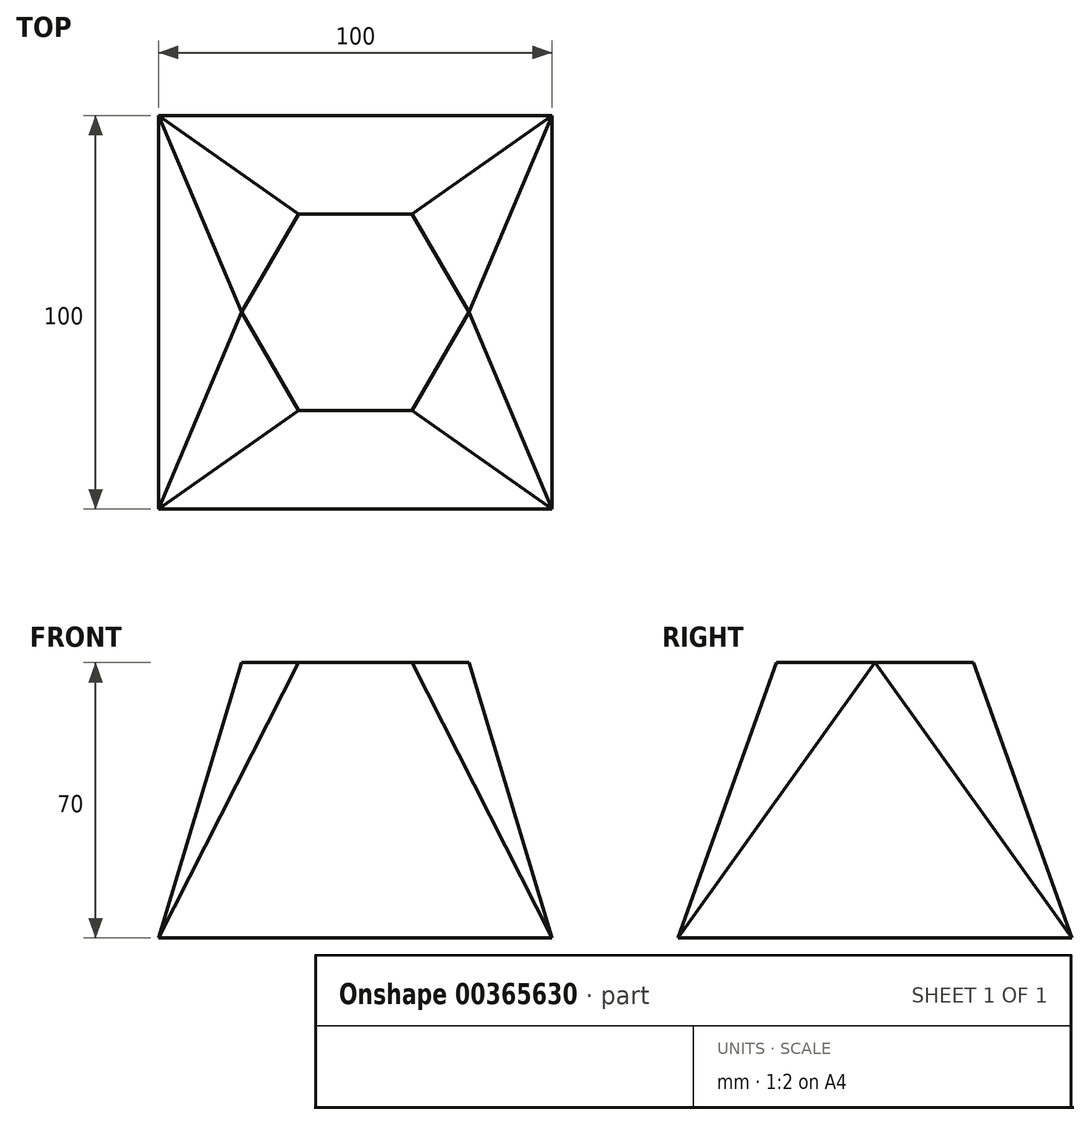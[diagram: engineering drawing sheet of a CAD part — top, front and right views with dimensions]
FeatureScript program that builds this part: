
annotation { "Feature Type Name" : "Feature", "Feature Type Description" : "" }
export const myFeature = defineFeature(function(context is Context, id is Id, definition is map)
    precondition{}
    {
        {
            var Q0;
            Q0=qCreatedBy(makeId("Top.planeOp"),FACE);
            cPlane(context, id + "F0", {"entities" : qUnion([Q0]), "cplaneType" : CPlaneType.OFFSET, "offset" : 70 * mm, "width" : 150 * mm, "height" : 150 * mm});
        }
        {
            var Q0;
            Q0=qCreatedBy(id+"F0.planeOp",FACE);
            var sketch = newSketch(context, id + "F1", { "sketchPlane" : qUnion([Q0])});
            skCircle(sketch, "E0.cCircle", {"center": v(0, 0) * mm, "radius": 25 * mm, "construction": true});
            skLineSegment(sketch, "E0.0", {"start": v(-14.43, 25) * mm, "end": v(14.43, 25) * mm});
            skLineSegment(sketch, "E0.1", {"start": v(14.43, 25) * mm, "end": v(28.87, 0) * mm});
            skLineSegment(sketch, "E0.2", {"start": v(28.87, 0) * mm, "end": v(14.43, -25) * mm});
            skLineSegment(sketch, "E0.3", {"start": v(14.43, -25) * mm, "end": v(-14.43, -25) * mm});
            skLineSegment(sketch, "E0.4", {"start": v(-14.43, -25) * mm, "end": v(-28.87, 0) * mm});
            skLineSegment(sketch, "E0.5", {"start": v(-28.87, 0) * mm, "end": v(-14.43, 25) * mm});
            skPoint(sketch, "E0.0.midPoint", {"position": v(0, 25) * mm});
            skLineSegment(sketch, "E1", {"start": v(-14.43, 25) * mm, "end": v(-14.43, -25) * mm});
            skLineSegment(sketch, "E2", {"start": v(14.43, 25) * mm, "end": v(14.43, -25) * mm});
            skSolve(sketch);
        }
        {
            var Q0;
            Q0=qCreatedBy(makeId("Top.planeOp"),FACE);
            var sketch = newSketch(context, id + "F2", { "sketchPlane" : qUnion([Q0])});
            skLineSegment(sketch, "E3.bottom", {"start": v(-50, 50) * mm, "end": v(50, 50) * mm});
            skLineSegment(sketch, "E3.top", {"start": v(-50, -50) * mm, "end": v(50, -50) * mm});
            skLineSegment(sketch, "E3.left", {"start": v(-50, 50) * mm, "end": v(-50, -50) * mm});
            skLineSegment(sketch, "E3.right", {"start": v(50, 50) * mm, "end": v(50, -50) * mm});
            skPoint(sketch, "E3.middle", {"position": v(0, 0) * mm});
            skSolve(sketch);
        }
        {
            var Q0;
            Q0=makeQuery(id+"F1.imprint","IMPRINT",FACE,{"disambiguationData":[TD([[makeQuery(id+"F1.imprint","IMPRINT",EDGE,{"derivedFrom":sQuery(id+"F1.wireOp",EDGE,"E0.0")}),-1.0]])]});
            var Q1;
            Q1=makeQuery(id+"F2.imprint","IMPRINT",FACE,{"disambiguationData":[TD([[makeQuery(id+"F2.imprint","IMPRINT",EDGE,{"derivedFrom":sQuery(id+"F2.wireOp",EDGE,"E3.bottom")}),-1.0]])]});
            loft(context, id + "F3", {"sheetProfilesArray" : [{ "sheetProfileEntities" : qUnion([Q0]) }, { "sheetProfileEntities" : qUnion([Q1]) }]});
        }
        {
            var Q1;
            Q1=makeQuery(id+"F1.imprint","IMPRINT",FACE,{"disambiguationData":[TD([[makeQuery(id+"F1.imprint","IMPRINT",EDGE,{"derivedFrom":sQuery(id+"F1.wireOp",EDGE,"E0.4")}),-1.0]])]});
            var Q2;
            Q2=makeQuery(id+"F3.opLoft","MID_CAP_VERTEX",VERTEX,{"disambiguationData":[OSD([sQuery(id+"F2.wireOp",EDGE,"E3.bottom"),sQuery(id+"F2.wireOp",EDGE,"E3.left")])],"capPos":1.0});
            loft(context, id + "F4", {"operationType" : NewBodyOperationType.ADD, "sheetProfilesArray" : [{ "sheetProfileEntities" : qUnion([Q1]) }, { "sheetProfileEntities" : qUnion([Q2]) }]});
        }
        {
            var Q1;
            Q1=makeQuery(id+"F4.opLoft","SWEPT_FACE",FACE,{"disambiguationData":[OSD([sQuery(id+"F1.wireOp",EDGE,"E0.3"),sQuery(id+"F1.wireOp",EDGE,"E0.4"),sQuery(id+"F1.wireOp",EDGE,"E0.5"),sQuery(id+"F1.wireOp",EDGE,"E1")])]});
            var Q2;
            Q2=makeQuery(id+"F3.opLoft","MID_CAP_VERTEX",VERTEX,{"disambiguationData":[OSD([sQuery(id+"F2.wireOp",EDGE,"E3.top"),sQuery(id+"F2.wireOp",EDGE,"E3.left")])],"capPos":1.0});
            loft(context, id + "F5", {"operationType" : NewBodyOperationType.ADD, "sheetProfilesArray" : [{ "sheetProfileEntities" : qUnion([Q1]) }, { "sheetProfileEntities" : qUnion([Q2]) }]});
        }
        {
            var Q1;
            Q1=makeQuery(id+"F1.imprint","IMPRINT",FACE,{"disambiguationData":[TD([[makeQuery(id+"F1.imprint","IMPRINT",EDGE,{"derivedFrom":sQuery(id+"F1.wireOp",EDGE,"E0.1")}),-1.0]])]});
            var Q2;
            Q2=makeQuery(id+"F3.opLoft","MID_CAP_VERTEX",VERTEX,{"disambiguationData":[OSD([sQuery(id+"F2.wireOp",EDGE,"E3.top"),sQuery(id+"F2.wireOp",EDGE,"E3.right")])],"capPos":1.0});
            loft(context, id + "F6", {"operationType" : NewBodyOperationType.ADD, "sheetProfilesArray" : [{ "sheetProfileEntities" : qUnion([Q1]) }, { "sheetProfileEntities" : qUnion([Q2]) }]});
        }
        {
            var Q1;
            Q1=makeQuery(id+"F6.opLoft","SWEPT_FACE",FACE,{"disambiguationData":[OSD([sQuery(id+"F1.wireOp",EDGE,"E0.0"),sQuery(id+"F1.wireOp",EDGE,"E0.1"),sQuery(id+"F1.wireOp",EDGE,"E0.2"),sQuery(id+"F1.wireOp",EDGE,"E2")])]});
            var Q2;
            Q2=makeQuery(id+"F3.opLoft","MID_CAP_VERTEX",VERTEX,{"disambiguationData":[OSD([sQuery(id+"F2.wireOp",EDGE,"E3.bottom"),sQuery(id+"F2.wireOp",EDGE,"E3.right")])],"capPos":1.0});
            loft(context, id + "F7", {"operationType" : NewBodyOperationType.ADD, "sheetProfilesArray" : [{ "sheetProfileEntities" : qUnion([Q1]) }, { "sheetProfileEntities" : qUnion([Q2]) }]});
        }
    });
